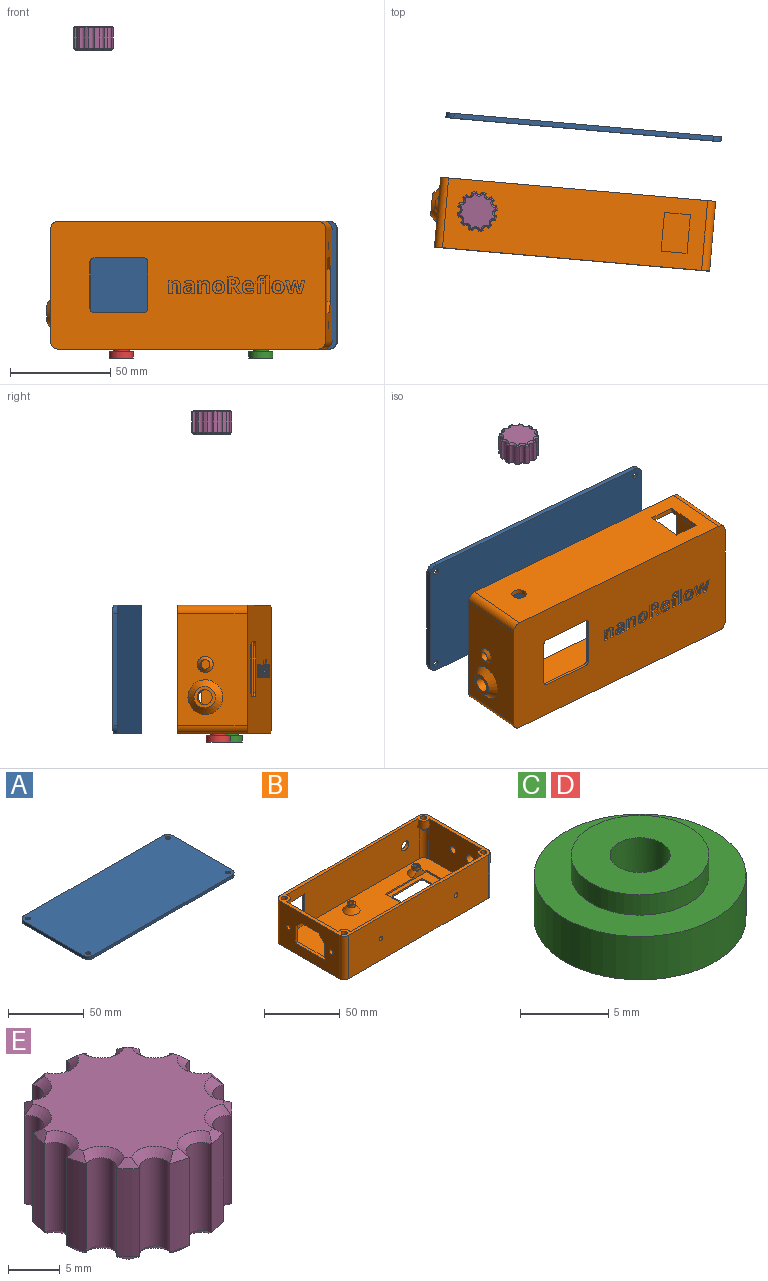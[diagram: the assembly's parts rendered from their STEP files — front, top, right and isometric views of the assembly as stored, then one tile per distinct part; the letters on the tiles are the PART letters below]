
ASSEMBLY  parts=5 mates=4
PART A: 18 faces, bbox 138x64x2.4 mm
  f0: plane 130x2.4mm, normal (0,-1,0), area 312mm2, adj f1,f7,f8,f9
  f1: cylinder r=4mm len=4mm, axis (0,0,-1), area 15.1mm2, adj f0,f2,f8,f9
  f2: plane 56x2.4mm, normal (1,0,0), area 134.4mm2, adj f1,f3,f8,f9
  f3: cylinder r=4mm len=4mm, axis (0,0,-1), area 15.1mm2, adj f2,f4,f8,f9
  f4: plane 130x2.4mm, normal (0,1,0), area 312mm2, adj f3,f5,f8,f9
  f5: cylinder r=4mm len=4mm, axis (0,0,-1), area 15.1mm2, adj f4,f6,f8,f9
  f6: plane 56x2.4mm, normal (-1,0,0), area 134.4mm2, adj f5,f7,f8,f9
  f7: cylinder r=4mm len=4mm, axis (0,0,-1), area 15.1mm2, adj f0,f6,f8,f9
  f8: plane 138x64mm, normal (0,0,1), area 8786.1mm2, adj f0,f1,f2,f3,f4,f5,f6,f7
  f9: plane 138x64mm, normal (0,0,-1), area 8723.2mm2, adj f0,f1,f2,f3,f4,f5,f6,f7
  f10: cylinder r=1.6mm len=3.2mm, axis (0,0,-1), area 12.6mm2, adj f8,f11
  f11: cone r=1.6mm half-angle=45deg, axis (0,0,-1), area 22.2mm2, adj f9,f10
  f12: cylinder r=1.6mm len=3.2mm, axis (0,0,-1), area 12.6mm2, adj f8,f13
  f13: cone r=1.6mm half-angle=45deg, axis (0,0,-1), area 22.2mm2, adj f9,f12
  f14: cylinder r=1.6mm len=3.2mm, axis (0,0,-1), area 12.6mm2, adj f8,f15
  f15: cone r=1.6mm half-angle=45deg, axis (0,0,-1), area 22.2mm2, adj f9,f14
  f16: cylinder r=1.6mm len=3.2mm, axis (0,0,-1), area 12.6mm2, adj f8,f17
  f17: cone r=1.6mm half-angle=45deg, axis (0,0,-1), area 22.2mm2, adj f9,f16
PART B: 289 faces, bbox 141.5x64.4x35.1 mm
  f0: plane 138x64mm, normal (0,0,-1), area 7748.2mm2, adj f9,f11,f12,f13,f14,f16,f17,f18
  f1: plane 125.33x32.73mm, normal (0,1,0), area 4045.5mm2, adj f3,f5,f10,f15,f69,f71,f73,f74
  f2: plane 51.33x32.73mm, normal (-1,0,0), area 1585.9mm2, adj f3,f7,f10,f15,f67,f71,f74,f75
  f3: cylinder r=4mm len=24.86mm, axis (0,0,-1), area 148.7mm2, adj f1,f2,f10,f72,f74
  f4: plane 51.33x32.73mm, normal (1,0,0), area 1139.5mm2, adj f5,f8,f10,f15,f49,f50,f51,f52
  f5: cylinder r=4mm len=24.86mm, axis (0,0,1), area 148.7mm2, adj f1,f4,f10,f70,f73
  f6: plane 125.33x32.73mm, normal (0,-1,0), area 3768.6mm2, adj f7,f8,f10,f15,f44,f45,f46,f47
  f7: cylinder r=4mm len=24.86mm, axis (0,0,1), area 148.7mm2, adj f2,f6,f10,f68,f75
  f8: cylinder r=4mm len=24.86mm, axis (0,0,-1), area 148.7mm2, adj f4,f6,f10,f66,f76
  f9: plane 130x35mm, normal (0,1,0), area 4257.1mm2, adj f0,f15,f44,f45,f46,f47,f48,f58
  f10: plane 133.2x59.2mm, normal (0,0,1), area 6216.1mm2, adj f1,f2,f3,f4,f5,f6,f7,f8
  f11: plane 25x1.2mm, normal (0,-1,0), area 30mm2, adj f0,f23,f61,f64
  f12: plane 23.4x1.2mm, normal (1,0,0), area 28.1mm2, adj f0,f23,f61,f62
  f13: plane 25x1.2mm, normal (0,1,0), area 30mm2, adj f0,f23,f62,f63
  f14: plane 23.4x1.2mm, normal (-1,0,0), area 28.1mm2, adj f0,f23,f63,f64
  f15: plane 138x64mm, normal (0,0,1), area 997.6mm2, adj f1,f2,f4,f6,f9,f16,f17,f18
  f16: plane 130x35mm, normal (0,-1,0), area 4533.9mm2, adj f0,f15,f57,f60,f282,f283
  f17: plane 56x35mm, normal (1,0,0), area 1672.1mm2, adj f0,f15,f57,f58,f287,f288
  f18: plane 56x35mm, normal (-1,0,0), area 1450.4mm2, adj f0,f15,f49,f50,f51,f52,f53,f54
  f19: plane 33.6x1.2mm, normal (-1,0,0), area 40.3mm2, adj f10,f20,f22,f23
  f20: plane 38.4x5.2mm, normal (0,-1,0), area 70.8mm2, adj f10,f19,f21,f23,f34
  f21: plane 33.6x1.2mm, normal (1,0,0), area 40.3mm2, adj f10,f20,f22,f23
  f22: plane 38.4x5.2mm, normal (0,1,0), area 70.8mm2, adj f10,f19,f21,f23,f33
  f23: plane 38.4x33.6mm, normal (0,0,1), area 499.1mm2, adj f11,f12,f13,f14,f19,f20,f21,f22
  f24: cylinder r=2.7mm len=5.4mm, axis (0,0,-1), area 33.9mm2, adj f25,f35
  f25: plane 5.4x5.4mm, normal (0,0,1), area 14.3mm2, adj f24,f43
  f26: cylinder r=2.7mm len=5.4mm, axis (0,0,-1), area 33.9mm2, adj f27,f32
  f27: plane 5.4x5.4mm, normal (0,0,1), area 14.3mm2, adj f26,f41
  f28: cylinder r=2.7mm len=5.4mm, axis (0,0,-1), area 33.9mm2, adj f29,f33
  f29: plane 5.4x5.4mm, normal (0,0,1), area 14.3mm2, adj f28,f39
  f30: cylinder r=2.7mm len=5.4mm, axis (0,0,-1), area 33.9mm2, adj f31,f34
  f31: plane 5.4x5.4mm, normal (0,0,1), area 14.3mm2, adj f30,f37
  f32: cone r=2.7mm half-angle=36.9deg, axis (0,0,-1), area 131.9mm2, adj f10,f26
  f33: cone r=2.7mm half-angle=36.9deg, axis (0,0,-1), area 96.2mm2, adj f10,f22,f28
  f34: cone r=2.7mm half-angle=36.9deg, axis (0,0,-1), area 96.2mm2, adj f10,f20,f30
  f35: cone r=2.7mm half-angle=36.9deg, axis (0,0,-1), area 131.9mm2, adj f10,f24
  f36: plane 3.3x3.3mm, normal (0,0,1), area 8.6mm2, adj f37
  f37: cylinder r=1.65mm len=6mm, axis (0,0,-1), area 62.2mm2, adj f31,f36
  f38: plane 3.3x3.3mm, normal (0,0,1), area 8.6mm2, adj f39
  f39: cylinder r=1.65mm len=6mm, axis (0,0,-1), area 62.2mm2, adj f29,f38
  f40: plane 3.3x3.3mm, normal (0,0,1), area 8.6mm2, adj f41
  f41: cylinder r=1.65mm len=6mm, axis (0,0,-1), area 62.2mm2, adj f27,f40
  f42: plane 3.3x3.3mm, normal (0,0,1), area 8.6mm2, adj f43
  f43: cylinder r=1.65mm len=6mm, axis (0,0,-1), area 62.2mm2, adj f25,f42
  f44: plane 13x2.4mm, normal (0,0,1), area 31.2mm2, adj f6,f9,f45,f47
  f45: plane 19.4x2.4mm, normal (1,0,0), area 46.6mm2, adj f6,f9,f44,f46
  f46: plane 13x2.4mm, normal (0,0,-1), area 31.2mm2, adj f6,f9,f45,f47
  f47: plane 19.4x2.4mm, normal (-1,0,0), area 46.6mm2, adj f6,f9,f44,f46
  f48: cylinder r=3.6mm len=7.2mm, axis (0,1,0), area 54.3mm2, adj f6,f9
  f49: plane 13.5x2.4mm, normal (0,-1,0), area 32.4mm2, adj f4,f18,f50,f54
  f50: plane 27.4x2.4mm, normal (0,0,1), area 65.8mm2, adj f4,f18,f49,f51
  f51: plane 13.5x2.4mm, normal (0,1,0), area 32.4mm2, adj f4,f18,f50,f52
  f52: plane 5.7x5.5mm, normal (0,0.69,-0.72), area 19mm2, adj f4,f18,f51,f53
  f53: plane 16x2.4mm, normal (0,0,-1), area 38.4mm2, adj f4,f18,f52,f54
  f54: plane 5.7x5.5mm, normal (0,-0.69,-0.72), area 19mm2, adj f4,f18,f49,f53
  f55: cylinder r=1.8mm len=3.6mm, axis (-1,0,0), area 27.1mm2, adj f4,f18
  f56: cylinder r=1.8mm len=3.6mm, axis (-1,0,0), area 27.1mm2, adj f4,f18
  f57: cylinder r=4mm len=35mm, axis (0,0,1), area 219.9mm2, adj f0,f15,f16,f17
  f58: cylinder r=4mm len=35mm, axis (0,0,-1), area 219.9mm2, adj f0,f9,f15,f17
  f59: cylinder r=4mm len=35mm, axis (0,0,1), area 219.9mm2, adj f0,f9,f15,f18
  f60: cylinder r=4mm len=35mm, axis (0,0,-1), area 219.9mm2, adj f0,f15,f16,f18
  f61: cylinder r=2mm len=2mm, axis (0,0,1), area 3.8mm2, adj f0,f11,f12,f23
  f62: cylinder r=2mm len=2mm, axis (0,0,-1), area 3.8mm2, adj f0,f12,f13,f23
  f63: cylinder r=2mm len=2mm, axis (0,0,1), area 3.8mm2, adj f0,f13,f14,f23
  f64: cylinder r=2mm len=2mm, axis (0,0,-1), area 3.8mm2, adj f0,f11,f14,f23
  f65: cylinder r=4.12mm len=6.5mm, axis (0,0,1), area 63.5mm2, adj f4,f6,f15,f76
  f66: plane 1.25x1.25mm, normal (0,0,-1), area 1.2mm2, adj f8,f76
  f67: cylinder r=4.12mm len=6.5mm, axis (0,0,1), area 63.5mm2, adj f2,f6,f15,f75
  f68: plane 1.25x1.25mm, normal (0,0,-1), area 1.2mm2, adj f7,f75
  f69: cylinder r=4.12mm len=6.5mm, axis (0,0,1), area 63.5mm2, adj f1,f4,f15,f73
  f70: plane 1.25x1.25mm, normal (0,0,-1), area 1.2mm2, adj f5,f73
  f71: cylinder r=4.12mm len=6.5mm, axis (0,0,1), area 63.5mm2, adj f1,f2,f15,f74
  f72: plane 1.25x1.25mm, normal (0,0,-1), area 1.2mm2, adj f3,f74
  f73: cone r=0.62mm half-angle=45deg, axis (0,0,1), area 34.3mm2, adj f1,f4,f5,f69,f70
  f74: cone r=4.12mm half-angle=45deg, axis (0,0,1), area 34.3mm2, adj f1,f2,f3,f71,f72
  f75: cone r=0.62mm half-angle=45deg, axis (0,0,1), area 34.3mm2, adj f2,f6,f7,f67,f68
  f76: cone r=4.12mm half-angle=45deg, axis (0,0,1), area 34.3mm2, adj f4,f6,f8,f65,f66
  f77: cone r=0mm half-angle=59deg, axis (0,0,1), area 14.7mm2, adj f78
  f78: cylinder r=2mm len=6mm, axis (0,0,1), area 75.4mm2, adj f15,f77
  f79: cone r=0mm half-angle=59deg, axis (0,0,1), area 14.7mm2, adj f80
  f80: cylinder r=2mm len=6mm, axis (0,0,1), area 75.4mm2, adj f15,f79
  f81: cone r=0mm half-angle=59deg, axis (0,0,1), area 14.7mm2, adj f82
  f82: cylinder r=2mm len=6mm, axis (0,0,1), area 75.4mm2, adj f15,f81
  f83: cone r=0mm half-angle=59deg, axis (0,0,1), area 14.7mm2, adj f84
  f84: cylinder r=2mm len=6mm, axis (0,0,1), area 75.4mm2, adj f15,f83
  f85: extruded ~2.4x1mm, area 2.6mm2, adj f0,f86,f104,f105
  f86: extruded ~1.26x1mm, area 1.3mm2, adj f0,f85,f87,f105
  f87: extruded ~1x0.97mm, area 1mm2, adj f0,f86,f88,f105
  f88: plane 1.34x1mm, normal (1,0,0), area 1.3mm2, adj f0,f87,f89,f105
  f89: extruded ~1.07x1mm, area 1.1mm2, adj f0,f88,f90,f105
  f90: extruded ~1.09x1mm, area 1.1mm2, adj f0,f89,f91,f105
  f91: extruded ~1.15x1mm, area 1.3mm2, adj f0,f90,f92,f105
  f92: extruded ~1.15x1mm, area 1.3mm2, adj f0,f91,f93,f105
  f93: plane 4.1x1mm, normal (0,1,0), area 4.1mm2, adj f0,f92,f94,f105
  f94: plane 1x0.84mm, normal (1,0,0), area 0.8mm2, adj f0,f93,f95,f105
  f95: extruded ~2.12x1mm, area 2.3mm2, adj f0,f94,f96,f105
  f96: extruded ~2.1x1mm, area 2.3mm2, adj f0,f95,f97,f105
  f97: extruded ~2.21x1mm, area 2.4mm2, adj f0,f96,f98,f105
  f98: extruded ~2.47x1mm, area 2.7mm2, adj f0,f97,f104,f105
  f99: extruded ~1x0.86mm, area 1mm2, adj f100,f103,f105,f106
  f100: extruded ~1x0.88mm, area 1mm2, adj f99,f101,f105,f106
  f101: extruded ~1x0.99mm, area 1.1mm2, adj f100,f102,f105,f106
  f102: plane 2.43x1mm, normal (0,-1,0), area 2.4mm2, adj f101,f103,f105,f106
  f103: extruded ~1x0.99mm, area 1.1mm2, adj f99,f102,f105,f106
  f104: extruded ~2.4x1mm, area 2.6mm2, adj f0,f85,f98,f105
  f105: plane 6.59x5.86mm, normal (0,0,-1), area 24.4mm2, adj f85,f86,f87,f88,f89,f90,f91,f92
  f106: plane 2.43x1.34mm, normal (0,0,-1), area 2.6mm2, adj f99,f100,f101,f102,f103
  f107: plane 3.19x1mm, normal (1,0,0), area 3.2mm2, adj f0,f108,f125,f126
  f108: plane 1x0.94mm, normal (0,1,0), area 0.9mm2, adj f0,f107,f109,f126
  f109: plane 3.19x1.99mm, normal (-0.85,0.53,0), area 3.8mm2, adj f0,f108,f110,f126
  f110: plane 1.96x1mm, normal (0,1,0), area 2mm2, adj f0,f109,f111,f126
  f111: extruded ~3.62x2.45mm, area 4.4mm2, adj f0,f110,f112,f126
  f112: extruded ~1.14x1mm, area 1.5mm2, adj f0,f111,f113,f126
  f113: extruded ~1.3x1mm, area 1.4mm2, adj f0,f112,f114,f126
  f114: extruded ~1.87x1mm, area 2.1mm2, adj f0,f113,f115,f126
  f115: extruded ~2.51x1mm, area 2.6mm2, adj f0,f114,f116,f126
  f116: plane 2.42x1mm, normal (0,-1,0), area 2.4mm2, adj f0,f115,f117,f126
  f117: plane 8.31x1mm, normal (-1,0,0), area 8.3mm2, adj f0,f116,f125,f126
  f118: plane 1x0.57mm, normal (0,-1,0), area 0.6mm2, adj f119,f124,f126,f127
  f119: plane 2.25x1mm, normal (1,0,0), area 2.2mm2, adj f118,f120,f126,f127
  f120: plane 1x0.54mm, normal (0,1,0), area 0.5mm2, adj f119,f121,f126,f127
  f121: extruded ~1.26x1mm, area 1.3mm2, adj f120,f122,f126,f127
  f122: extruded ~1x0.84mm, area 1mm2, adj f121,f123,f126,f127
  f123: extruded ~1x0.88mm, area 1mm2, adj f122,f124,f126,f127
  f124: extruded ~1.23x1mm, area 1.3mm2, adj f118,f123,f126,f127
  f125: plane 1.76x1mm, normal (0,1,0), area 1.8mm2, adj f0,f107,f117,f126
  f126: plane 8.31x6.64mm, normal (0,0,-1), area 33.7mm2, adj f107,f108,f109,f110,f111,f112,f113,f114
  f127: plane 2.25x2.2mm, normal (0,0,-1), area 4.4mm2, adj f118,f119,f120,f121,f122,f123,f124
  f128: extruded ~2.43x1mm, area 2.6mm2, adj f0,f129,f145,f146
  f129: extruded ~1.75x1mm, area 1.8mm2, adj f0,f128,f130,f146
  f130: extruded ~1.14x1.07mm, area 1.6mm2, adj f0,f129,f131,f146
  f131: extruded ~1.62x1mm, area 1.7mm2, adj f0,f130,f132,f146
  f132: extruded ~2.29x1mm, area 2.5mm2, adj f0,f131,f133,f146
  f133: extruded ~2.42x1mm, area 2.6mm2, adj f0,f132,f134,f146
  f134: extruded ~1.75x1mm, area 1.8mm2, adj f0,f133,f135,f146
  f135: extruded ~1.15x1.07mm, area 1.6mm2, adj f0,f134,f136,f146
  f136: extruded ~1.62x1mm, area 1.7mm2, adj f0,f135,f145,f146
  f137: extruded ~1.43x1mm, area 1.5mm2, adj f138,f144,f146,f147
  f138: extruded ~1.42x1mm, area 1.5mm2, adj f137,f139,f146,f147
  f139: extruded ~1x1mm, area 1.2mm2, adj f138,f140,f146,f147
  f140: extruded ~1.01x1mm, area 1.2mm2, adj f139,f141,f146,f147
  f141: extruded ~1.42x1mm, area 1.5mm2, adj f140,f142,f146,f147
  f142: extruded ~1.43x1mm, area 1.5mm2, adj f141,f143,f146,f147
  f143: extruded ~1x1mm, area 1.2mm2, adj f142,f144,f146,f147
  f144: extruded ~1.01x1mm, area 1.2mm2, adj f137,f143,f146,f147
  f145: extruded ~2.28x1mm, area 2.5mm2, adj f0,f128,f136,f146
  f146: plane 6.59x6.16mm, normal (0,0,-1), area 24.7mm2, adj f128,f129,f130,f131,f132,f133,f134,f135
  f147: plane 3.8x2.62mm, normal (0,0,-1), area 8.4mm2, adj f137,f138,f139,f140,f141,f142,f143,f144
  f148: plane 1x0.67mm, normal (0.04,1,0), area 0.7mm2, adj f149,f172,f173,f281
  f149: plane 1x0.52mm, normal (-1,0,0), area 0.5mm2, adj f148,f150,f173,f281
  f150: extruded ~1x0.92mm, area 1mm2, adj f149,f151,f173,f281
  f151: extruded ~1x0.97mm, area 1.1mm2, adj f150,f152,f173,f281
  f152: extruded ~1x0.84mm, area 1.3mm2, adj f151,f153,f173,f281
  f153: extruded ~1x0.76mm, area 0.9mm2, adj f152,f172,f173,f281
  f154: plane 1x0.86mm, normal (-0.93,0.36,0), area 0.9mm2, adj f0,f155,f171,f173
  f155: plane 1.21x1mm, normal (0,1,0), area 1.2mm2, adj f0,f154,f156,f173
  f156: plane 4.24x1mm, normal (1,0,0), area 4.2mm2, adj f0,f155,f157,f173
  f157: extruded ~1.7x1mm, area 1.9mm2, adj f0,f156,f158,f173
  f158: extruded ~1.96x1mm, area 2.1mm2, adj f0,f157,f159,f173
  f159: extruded ~2.43x1mm, area 2.5mm2, adj f0,f158,f160,f173
  f160: plane 1.17x1mm, normal (-0.9,0.44,0), area 1.3mm2, adj f0,f159,f161,f173
  f161: extruded ~1.79x1mm, area 1.9mm2, adj f0,f160,f162,f173
  f162: extruded ~1x0.99mm, area 1.6mm2, adj f0,f161,f163,f173
  f163: plane 1x0.28mm, normal (-1,0,0), area 0.3mm2, adj f0,f162,f164,f173
  f164: plane 1.1x1mm, normal (-0.03,-1,0), area 1.1mm2, adj f0,f163,f165,f173
  f165: extruded ~2.13x1mm, area 2.2mm2, adj f0,f164,f166,f173
  f166: extruded ~1.49x1mm, area 1.7mm2, adj f0,f165,f167,f173
  f167: extruded ~1.49x1mm, area 1.6mm2, adj f0,f166,f168,f173
  f168: extruded ~1.44x1mm, area 1.6mm2, adj f0,f167,f169,f173
  f169: extruded ~1.21x1mm, area 1.2mm2, adj f0,f168,f170,f173
  f170: extruded ~1x0.9mm, area 1.2mm2, adj f0,f169,f171,f173
  f171: plane 1x0.05mm, normal (0,1,0), area 0mm2, adj f0,f154,f170,f173
  f172: extruded ~1.13x1mm, area 1.2mm2, adj f148,f153,f173,f281
  f173: plane 6.6x5.67mm, normal (0,0,-1), area 24.8mm2, adj f148,f149,f150,f151,f152,f153,f154,f155
  f174: plane 2.22x1mm, normal (-0.98,0.21,0), area 2.3mm2, adj f0,f175,f199,f200
  f175: plane 1.89x1mm, normal (0,1,0), area 1.9mm2, adj f0,f174,f176,f200
  f176: plane 6.36x1.83mm, normal (0.96,0.28,0), area 6.6mm2, adj f0,f175,f177,f200
  f177: plane 1.7x1mm, normal (0,-1,0), area 1.7mm2, adj f0,f176,f178,f200
  f178: plane 2.81x1mm, normal (-0.97,-0.26,0), area 2.9mm2, adj f0,f177,f179,f200
  f179: extruded ~1x0.96mm, area 1mm2, adj f0,f178,f180,f200
  f180: extruded ~1.12x1mm, area 1.1mm2, adj f0,f179,f181,f200
  f181: plane 1x0.03mm, normal (0,-1,0), area 0mm2, adj f0,f180,f182,f200
  f182: extruded ~1x0.42mm, area 0.4mm2, adj f0,f181,f183,f200
  f183: extruded ~1x0.54mm, area 0.5mm2, adj f0,f182,f184,f200
  f184: extruded ~1x0.52mm, area 0.5mm2, adj f0,f183,f185,f200
  f185: extruded ~1x0.37mm, area 0.4mm2, adj f0,f184,f186,f200
  f186: plane 3.05x1mm, normal (0.97,-0.24,0), area 3.1mm2, adj f0,f185,f187,f200
  f187: plane 1.91x1mm, normal (0,-1,0), area 1.9mm2, adj f0,f186,f188,f200
  f188: plane 3.05x1mm, normal (-0.97,-0.25,0), area 3.1mm2, adj f0,f187,f189,f200
  f189: plane 1x0.48mm, normal (-0.98,-0.18,0), area 0.5mm2, adj f0,f188,f190,f200
  f190: extruded ~1.37x1mm, area 1.4mm2, adj f0,f189,f191,f200
  f191: plane 1x0.03mm, normal (0,-1,0), area 0mm2, adj f0,f190,f192,f200
  f192: extruded ~2.09x1mm, area 2.1mm2, adj f0,f191,f193,f200
  f193: plane 2.81x1mm, normal (0.97,-0.25,0), area 2.9mm2, adj f0,f192,f194,f200
  f194: plane 1.73x1mm, normal (0,-1,0), area 1.7mm2, adj f0,f193,f195,f200
  f195: plane 6.36x1.81mm, normal (-0.96,0.27,0), area 6.6mm2, adj f0,f194,f196,f200
  f196: plane 1.87x1mm, normal (0,1,0), area 1.9mm2, adj f0,f195,f197,f200
  f197: plane 5.03x1.16mm, normal (0.97,0.22,0), area 5.2mm2, adj f0,f196,f198,f200
  f198: plane 1x0.04mm, normal (0,1,0), area 0mm2, adj f0,f197,f199,f200
  f199: plane 2.81x1mm, normal (-0.97,0.23,0), area 2.9mm2, adj f0,f174,f198,f200
  f200: plane 9.74x6.36mm, normal (0,0,-1), area 34.5mm2, adj f174,f175,f176,f177,f178,f179,f180,f181
  f201: plane 1.73x1mm, normal (0,1,0), area 1.7mm2, adj f0,f202,f204,f205
  f202: plane 8.85x1mm, normal (1,0,0), area 8.8mm2, adj f0,f201,f203,f205
  f203: plane 1.73x1mm, normal (0,-1,0), area 1.7mm2, adj f0,f202,f204,f205
  f204: plane 8.85x1mm, normal (-1,0,0), area 8.8mm2, adj f0,f201,f203,f205
  f205: plane 8.85x1.73mm, normal (0,0,-1), area 15.3mm2, adj f201,f202,f203,f204
  f206: plane 1.5x1mm, normal (0,1,0), area 1.5mm2, adj f0,f207,f223,f224
  f207: plane 1.3x1mm, normal (1,0,0), area 1.3mm2, adj f0,f206,f208,f224
  f208: plane 1.5x1mm, normal (0,-1,0), area 1.5mm2, adj f0,f207,f209,f224
  f209: plane 1x0.4mm, normal (1,0,0), area 0.4mm2, adj f0,f208,f210,f224
  f210: extruded ~1x0.56mm, area 0.6mm2, adj f0,f209,f211,f224
  f211: extruded ~1x0.54mm, area 0.6mm2, adj f0,f210,f212,f224
  f212: extruded ~1x0.97mm, area 1mm2, adj f0,f211,f213,f224
  f213: plane 1.27x1mm, normal (0.94,0.33,0), area 1.3mm2, adj f0,f212,f214,f224
  f214: extruded ~1.6x1mm, area 1.6mm2, adj f0,f213,f215,f224
  f215: extruded ~1.71x1mm, area 1.8mm2, adj f0,f214,f216,f224
  f216: extruded ~1.59x1mm, area 1.7mm2, adj f0,f215,f217,f224
  f217: plane 1x0.47mm, normal (-1,0,0), area 0.5mm2, adj f0,f216,f218,f224
  f218: plane 1x0.96mm, normal (-0.44,-0.9,0), area 1.1mm2, adj f0,f217,f219,f224
  f219: plane 1x0.84mm, normal (-1,0,0), area 0.8mm2, adj f0,f218,f220,f224
  f220: plane 1x0.96mm, normal (0,1,0), area 1mm2, adj f0,f219,f221,f224
  f221: plane 5.05x1mm, normal (-1,0,0), area 5.1mm2, adj f0,f220,f222,f224
  f222: plane 1.73x1mm, normal (0,1,0), area 1.7mm2, adj f0,f221,f223,f224
  f223: plane 5.05x1mm, normal (1,0,0), area 5.1mm2, adj f0,f206,f222,f224
  f224: plane 8.91x4.8mm, normal (0,0,-1), area 20.4mm2, adj f206,f207,f208,f209,f210,f211,f212,f213
  f225: plane 1.73x1mm, normal (0,1,0), area 1.7mm2, adj f0,f226,f241,f242
  f226: plane 4.15x1mm, normal (1,0,0), area 4.1mm2, adj f0,f225,f227,f242
  f227: extruded ~1.73x1mm, area 1.9mm2, adj f0,f226,f228,f242
  f228: extruded ~1.68x1mm, area 1.8mm2, adj f0,f227,f229,f242
  f229: extruded ~1.16x1mm, area 1.2mm2, adj f0,f228,f230,f242
  f230: extruded ~1x0.8mm, area 1.1mm2, adj f0,f229,f231,f242
  f231: plane 1x0.1mm, normal (0,-1,0), area 0.1mm2, adj f0,f230,f232,f242
  f232: plane 1x0.81mm, normal (0.96,-0.28,0), area 0.8mm2, adj f0,f231,f233,f242
  f233: plane 1.32x1mm, normal (0,-1,0), area 1.3mm2, adj f0,f232,f234,f242
  f234: plane 6.36x1mm, normal (-1,0,0), area 6.4mm2, adj f0,f233,f235,f242
  f235: plane 1.73x1mm, normal (0,1,0), area 1.7mm2, adj f0,f234,f236,f242
  f236: plane 2.99x1mm, normal (1,0,0), area 3mm2, adj f0,f235,f237,f242
  f237: extruded ~1.61x1mm, area 1.7mm2, adj f0,f236,f238,f242
  f238: extruded ~1.05x1mm, area 1.2mm2, adj f0,f237,f239,f242
  f239: extruded ~1x0.78mm, area 0.9mm2, adj f0,f238,f240,f242
  f240: extruded ~1.03x1mm, area 1.1mm2, adj f0,f239,f241,f242
  f241: plane 3.71x1mm, normal (-1,0,0), area 3.7mm2, adj f0,f225,f240,f242
  f242: plane 6.48x5.87mm, normal (0,0,-1), area 24.7mm2, adj f225,f226,f227,f228,f229,f230,f231,f232
  f243: extruded ~2.43x1mm, area 2.6mm2, adj f0,f244,f260,f261
  f244: extruded ~1.75x1mm, area 1.8mm2, adj f0,f243,f245,f261
  f245: extruded ~1.14x1.07mm, area 1.6mm2, adj f0,f244,f246,f261
  f246: extruded ~1.62x1mm, area 1.7mm2, adj f0,f245,f247,f261
  f247: extruded ~2.29x1mm, area 2.5mm2, adj f0,f246,f248,f261
  f248: extruded ~2.42x1mm, area 2.6mm2, adj f0,f247,f249,f261
  f249: extruded ~1.75x1mm, area 1.8mm2, adj f0,f248,f250,f261
  f250: extruded ~1.15x1.07mm, area 1.6mm2, adj f0,f249,f251,f261
  f251: extruded ~1.62x1mm, area 1.7mm2, adj f0,f250,f260,f261
  f252: extruded ~1.43x1mm, area 1.5mm2, adj f253,f259,f261,f262
  f253: extruded ~1.42x1mm, area 1.5mm2, adj f252,f254,f261,f262
  f254: extruded ~1x1mm, area 1.2mm2, adj f253,f255,f261,f262
  f255: extruded ~1.01x1mm, area 1.2mm2, adj f254,f256,f261,f262
  f256: extruded ~1.42x1mm, area 1.5mm2, adj f255,f257,f261,f262
  f257: extruded ~1.43x1mm, area 1.5mm2, adj f256,f258,f261,f262
  f258: extruded ~1x1mm, area 1.2mm2, adj f257,f259,f261,f262
  f259: extruded ~1.01x1mm, area 1.2mm2, adj f252,f258,f261,f262
  f260: extruded ~2.28x1mm, area 2.5mm2, adj f0,f243,f251,f261
  f261: plane 6.59x6.16mm, normal (0,0,-1), area 24.7mm2, adj f243,f244,f245,f246,f247,f248,f249,f250
  f262: plane 3.8x2.62mm, normal (0,0,-1), area 8.4mm2, adj f252,f253,f254,f255,f256,f257,f258,f259
  f263: plane 1.73x1mm, normal (0,1,0), area 1.7mm2, adj f0,f264,f279,f280
  f264: plane 4.15x1mm, normal (1,0,0), area 4.1mm2, adj f0,f263,f265,f280
  f265: extruded ~1.73x1mm, area 1.9mm2, adj f0,f264,f266,f280
  f266: extruded ~1.68x1mm, area 1.8mm2, adj f0,f265,f267,f280
  f267: extruded ~1.16x1mm, area 1.2mm2, adj f0,f266,f268,f280
  f268: extruded ~1x0.8mm, area 1.1mm2, adj f0,f267,f269,f280
  f269: plane 1x0.1mm, normal (0,-1,0), area 0.1mm2, adj f0,f268,f270,f280
  f270: plane 1x0.81mm, normal (0.96,-0.28,0), area 0.8mm2, adj f0,f269,f271,f280
  f271: plane 1.32x1mm, normal (0,-1,0), area 1.3mm2, adj f0,f270,f272,f280
  f272: plane 6.36x1mm, normal (-1,0,0), area 6.4mm2, adj f0,f271,f273,f280
  f273: plane 1.73x1mm, normal (0,1,0), area 1.7mm2, adj f0,f272,f274,f280
  f274: plane 2.99x1mm, normal (1,0,0), area 3mm2, adj f0,f273,f275,f280
  f275: extruded ~1.61x1mm, area 1.7mm2, adj f0,f274,f276,f280
  f276: extruded ~1.05x1mm, area 1.2mm2, adj f0,f275,f277,f280
  f277: extruded ~1x0.78mm, area 0.9mm2, adj f0,f276,f278,f280
  f278: extruded ~1.03x1mm, area 1.1mm2, adj f0,f277,f279,f280
  f279: plane 3.71x1mm, normal (-1,0,0), area 3.7mm2, adj f0,f263,f278,f280
  f280: plane 6.48x5.87mm, normal (0,0,-1), area 24.7mm2, adj f263,f264,f265,f266,f267,f268,f269,f270
  f281: plane 2.17x1.79mm, normal (0,0,-1), area 3.1mm2, adj f148,f149,f150,f151,f152,f153,f172
  f282: cylinder r=1.6mm len=3.2mm, axis (0,-1,0), area 24.1mm2, adj f1,f16
  f283: cylinder r=1.6mm len=3.2mm, axis (0,-1,0), area 24.1mm2, adj f1,f16
  f284: cylinder r=2.46mm len=4.92mm, axis (1,0,0), area 60.8mm2, adj f2,f287
  f285: cylinder r=3.75mm len=7.5mm, axis (1,0,0), area 134.3mm2, adj f2,f286
  f286: plane 10.8x10.8mm, normal (1,0,0), area 47.4mm2, adj f285,f288
  f287: cone r=0.69mm half-angle=45deg, axis (-1,0,0), area 44mm2, adj f17,f284
  f288: cone r=5.4mm half-angle=45deg, axis (-1,0,0), area 206.7mm2, adj f17,f286
PART C: 7 faces, bbox 12x12x4.4 mm
  f0: cylinder r=6mm len=12mm, axis (0,0,-1), area 113.1mm2, adj f1,f2
  f1: plane 12x12mm, normal (0,0,1), area 65.3mm2, adj f0,f3
  f2: plane 12x12mm, normal (0,0,-1), area 88.5mm2, adj f0,f6
  f3: cylinder r=3.9mm len=7.8mm, axis (0,0,-1), area 34.3mm2, adj f1,f4
  f4: plane 7.8x7.8mm, normal (0,0,1), area 38.7mm2, adj f3,f5
  f5: cylinder r=1.7mm len=3.4mm, axis (0,0,-1), area 35.2mm2, adj f4,f6
  f6: cone r=1.7mm half-angle=45deg, axis (0,0,-1), area 22mm2, adj f2,f5
PART D: same geometry as C
PART E: 77 faces, bbox 19.8x19.8x12 mm
  f0: cylinder r=10mm len=10.4mm, axis (0,0,-1), area 23.2mm2, adj f25,f27,f28,f53
  f1: cylinder r=10mm len=10.4mm, axis (0,0,-1), area 23.2mm2, adj f26,f27,f31,f56
  f2: cylinder r=10mm len=10.4mm, axis (0,0,-1), area 23.2mm2, adj f19,f26,f35,f60
  f3: cylinder r=10mm len=10.4mm, axis (0,0,-1), area 23.2mm2, adj f20,f25,f32,f57
  f4: cylinder r=10mm len=10.4mm, axis (0,0,-1), area 23.2mm2, adj f17,f24,f47,f72
  f5: cylinder r=10mm len=10.4mm, axis (0,0,-1), area 23.2mm2, adj f23,f24,f51,f76
  f6: cylinder r=10mm len=10.4mm, axis (0,0,-1), area 23.2mm2, adj f22,f23,f48,f73
  f7: cylinder r=10mm len=10.4mm, axis (0,0,-1), area 23.2mm2, adj f21,f22,f44,f69
  f8: cylinder r=10mm len=10.4mm, axis (0,0,-1), area 23.2mm2, adj f16,f21,f40,f65
  f9: cylinder r=10mm len=10.4mm, axis (0,0,-1), area 23.2mm2, adj f16,f20,f36,f61
  f10: cylinder r=10mm len=10.4mm, axis (0,0,-1), area 23.2mm2, adj f18,f19,f39,f64
  f11: cylinder r=10mm len=10.4mm, axis (0,0,-1), area 23.2mm2, adj f17,f18,f43,f68
  f12: plane 17.94x17.94mm, normal (0,0,-1), area 168.2mm2, adj f28,f29,f30,f31,f32,f33,f34,f35
  f13: plane 17.94x17.94mm, normal (0,0,1), area 213.5mm2, adj f53,f54,f55,f56,f57,f58,f59,f60
  f14: cylinder r=3mm len=6mm, axis (0,0,-1), area 98mm2, adj f15,f52
  f15: plane 6x6mm, normal (0,0,-1), area 28.3mm2, adj f14
  f16: cylinder r=1.5mm len=10.4mm, axis (0,0,-1), area 46.7mm2, adj f8,f9,f38,f63
  f17: cylinder r=1.5mm len=10.4mm, axis (0,0,-1), area 46.7mm2, adj f4,f11,f45,f70
  f18: cylinder r=1.5mm len=10.4mm, axis (0,0,-1), area 46.7mm2, adj f10,f11,f41,f66
  f19: cylinder r=1.5mm len=10.4mm, axis (0,0,-1), area 46.7mm2, adj f2,f10,f37,f62
  f20: cylinder r=1.5mm len=10.4mm, axis (0,0,-1), area 46.7mm2, adj f3,f9,f34,f59
  f21: cylinder r=1.5mm len=10.4mm, axis (0,0,-1), area 46.7mm2, adj f7,f8,f42,f67
  f22: cylinder r=1.5mm len=10.4mm, axis (0,0,-1), area 46.7mm2, adj f6,f7,f46,f71
  f23: cylinder r=1.5mm len=10.4mm, axis (0,0,-1), area 46.7mm2, adj f5,f6,f50,f75
  f24: cylinder r=1.5mm len=10.4mm, axis (0,0,-1), area 46.7mm2, adj f4,f5,f49,f74
  f25: cylinder r=1.5mm len=10.4mm, axis (0,0,-1), area 46.7mm2, adj f0,f3,f30,f55
  f26: cylinder r=1.5mm len=10.4mm, axis (0,0,-1), area 46.7mm2, adj f1,f2,f33,f58
  f27: cylinder r=1.5mm len=10.4mm, axis (0,0,-1), area 46.7mm2, adj f0,f1,f29,f54
  f28: cone r=10mm half-angle=45deg, axis (0,0,1), area 1.6mm2, adj f0,f12,f29,f30
  f29: cone r=2.3mm half-angle=45deg, axis (0,0,-1), area 5.5mm2, adj f12,f27,f28,f31
  f30: cone r=2.3mm half-angle=45deg, axis (0,0,-1), area 5.5mm2, adj f12,f25,f28,f32
  f31: cone r=10mm half-angle=45deg, axis (0,0,1), area 1.6mm2, adj f1,f12,f29,f33
  f32: cone r=10mm half-angle=45deg, axis (0,0,1), area 1.6mm2, adj f3,f12,f30,f34
  f33: cone r=2.3mm half-angle=45deg, axis (0,0,-1), area 5.5mm2, adj f12,f26,f31,f35
  f34: cone r=2.3mm half-angle=45deg, axis (0,0,-1), area 5.5mm2, adj f12,f20,f32,f36
  f35: cone r=10mm half-angle=45deg, axis (0,0,1), area 1.6mm2, adj f2,f12,f33,f37
  f36: cone r=10mm half-angle=45deg, axis (0,0,1), area 1.6mm2, adj f9,f12,f34,f38
  f37: cone r=2.3mm half-angle=45deg, axis (0,0,-1), area 5.5mm2, adj f12,f19,f35,f39
  f38: cone r=2.3mm half-angle=45deg, axis (0,0,-1), area 5.5mm2, adj f12,f16,f36,f40
  f39: cone r=10mm half-angle=45deg, axis (0,0,1), area 1.6mm2, adj f10,f12,f37,f41
  f40: cone r=10mm half-angle=45deg, axis (0,0,1), area 1.6mm2, adj f8,f12,f38,f42
  f41: cone r=2.3mm half-angle=45deg, axis (0,0,-1), area 5.5mm2, adj f12,f18,f39,f43
  f42: cone r=2.3mm half-angle=45deg, axis (0,0,-1), area 5.5mm2, adj f12,f21,f40,f44
  f43: cone r=10mm half-angle=45deg, axis (0,0,1), area 1.6mm2, adj f11,f12,f41,f45
  f44: cone r=10mm half-angle=45deg, axis (0,0,1), area 1.6mm2, adj f7,f12,f42,f46
  f45: cone r=2.3mm half-angle=45deg, axis (0,0,-1), area 5.5mm2, adj f12,f17,f43,f47
  f46: cone r=2.3mm half-angle=45deg, axis (0,0,-1), area 5.5mm2, adj f12,f22,f44,f48
  f47: cone r=10mm half-angle=45deg, axis (0,0,1), area 1.6mm2, adj f4,f12,f45,f49
  f48: cone r=10mm half-angle=45deg, axis (0,0,1), area 1.6mm2, adj f6,f12,f46,f50
  f49: cone r=2.3mm half-angle=45deg, axis (0,0,-1), area 5.5mm2, adj f12,f24,f47,f51
  f50: cone r=2.3mm half-angle=45deg, axis (0,0,-1), area 5.5mm2, adj f12,f23,f48,f51
  f51: cone r=10mm half-angle=45deg, axis (0,0,1), area 1.6mm2, adj f5,f12,f49,f50
  f52: cone r=3.8mm half-angle=45deg, axis (0,0,-1), area 24.2mm2, adj f12,f14
  f53: cone r=9.2mm half-angle=45deg, axis (0,0,-1), area 1.6mm2, adj f0,f13,f54,f55
  f54: cone r=2.3mm half-angle=45deg, axis (0,0,1), area 5.5mm2, adj f13,f27,f53,f56
  f55: cone r=2.3mm half-angle=45deg, axis (0,0,1), area 5.5mm2, adj f13,f25,f53,f57
  f56: cone r=9.2mm half-angle=45deg, axis (0,0,-1), area 1.6mm2, adj f1,f13,f54,f58
  f57: cone r=9.2mm half-angle=45deg, axis (0,0,-1), area 1.6mm2, adj f3,f13,f55,f59
  f58: cone r=2.3mm half-angle=45deg, axis (0,0,1), area 5.5mm2, adj f13,f26,f56,f60
  f59: cone r=2.3mm half-angle=45deg, axis (0,0,1), area 5.5mm2, adj f13,f20,f57,f61
  f60: cone r=9.2mm half-angle=45deg, axis (0,0,-1), area 1.6mm2, adj f2,f13,f58,f62
  f61: cone r=9.2mm half-angle=45deg, axis (0,0,-1), area 1.6mm2, adj f9,f13,f59,f63
  f62: cone r=2.3mm half-angle=45deg, axis (0,0,1), area 5.5mm2, adj f13,f19,f60,f64
  f63: cone r=2.3mm half-angle=45deg, axis (0,0,1), area 5.5mm2, adj f13,f16,f61,f65
  f64: cone r=9.2mm half-angle=45deg, axis (0,0,-1), area 1.6mm2, adj f10,f13,f62,f66
  f65: cone r=9.2mm half-angle=45deg, axis (0,0,-1), area 1.6mm2, adj f8,f13,f63,f67
  f66: cone r=2.3mm half-angle=45deg, axis (0,0,1), area 5.5mm2, adj f13,f18,f64,f68
  f67: cone r=2.3mm half-angle=45deg, axis (0,0,1), area 5.5mm2, adj f13,f21,f65,f69
  f68: cone r=9.2mm half-angle=45deg, axis (0,0,-1), area 1.6mm2, adj f11,f13,f66,f70
  f69: cone r=9.2mm half-angle=45deg, axis (0,0,-1), area 1.6mm2, adj f7,f13,f67,f71
  f70: cone r=2.3mm half-angle=45deg, axis (0,0,1), area 5.5mm2, adj f13,f17,f68,f72
  f71: cone r=2.3mm half-angle=45deg, axis (0,0,1), area 5.5mm2, adj f13,f22,f69,f73
  f72: cone r=9.2mm half-angle=45deg, axis (0,0,-1), area 1.6mm2, adj f4,f13,f70,f74
  f73: cone r=9.2mm half-angle=45deg, axis (0,0,-1), area 1.6mm2, adj f6,f13,f71,f75
  f74: cone r=2.3mm half-angle=45deg, axis (0,0,1), area 5.5mm2, adj f13,f24,f72,f76
  f75: cone r=2.3mm half-angle=45deg, axis (0,0,1), area 5.5mm2, adj f13,f23,f73,f76
  f76: cone r=9.2mm half-angle=45deg, axis (0,0,-1), area 1.6mm2, adj f5,f13,f74,f75
PLACE A rot(axis=(1,-0.04,-0.04),90.1deg) t=(-57.01,121.94,-13.41)mm
PLACE B rot(axis=(0.03,0.71,0.71),176.5deg) t=(-65.93,19.93,-13.41)mm fixed
PLACE C rot(axis=(0,0,-1),5deg) t=(-29.54,34.32,-49.81)mm
PLACE D rot(axis=(0,0,-1),5deg) t=(-99.27,40.42,-49.81)mm
PLACE E rot(axis=(0,0,-1),5deg) t=(-113.25,43.55,104.14)mm
MATE slider B.f59 <-> A.f3  axis (0.09,1,0) through (1.87,49.14,14.59)mm
MATE slider C.f5 <-> B.f283  axis (0,0,1) through (-29.54,34.32,-45.41)mm
MATE slider E.f14 <-> B.f48  axis (0,0,1) through (-113.25,43.55,104.94)mm
MATE slider D.f3 <-> B.f282  axis (0,0,1) through (-99.27,40.42,-45.41)mm
